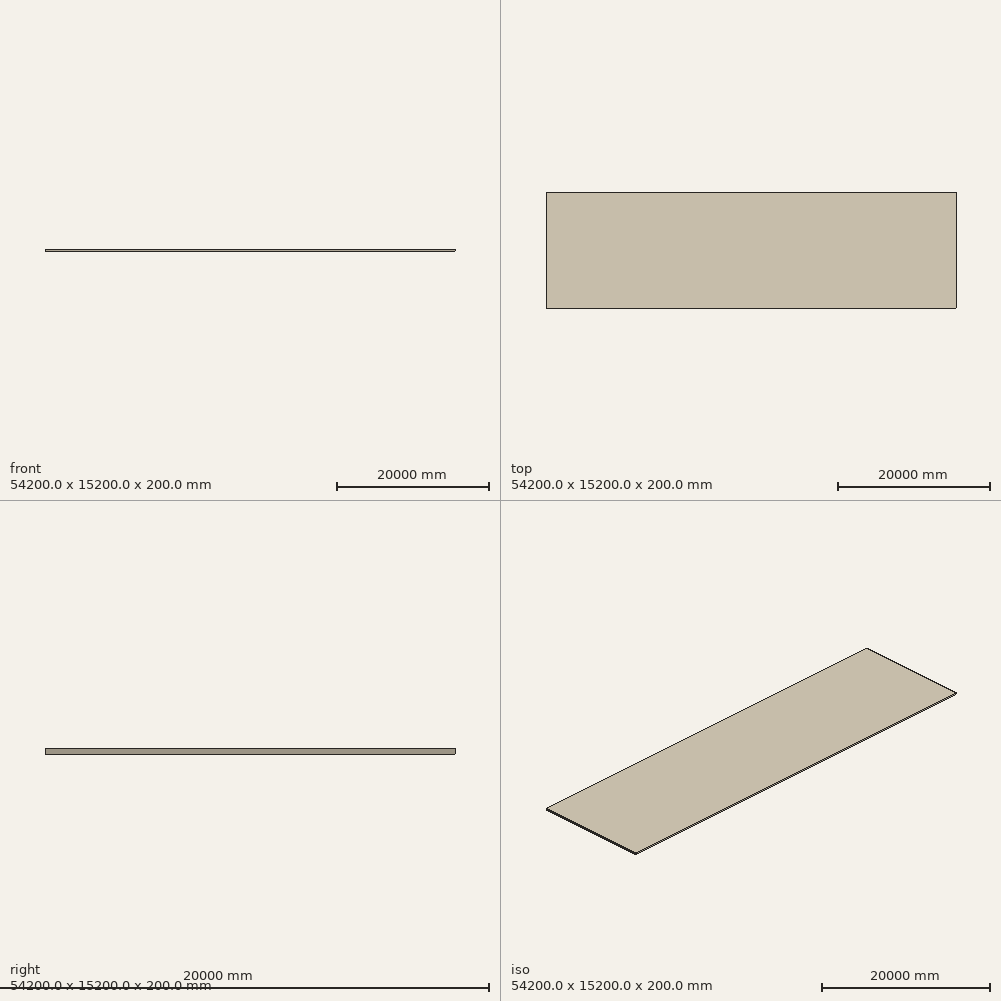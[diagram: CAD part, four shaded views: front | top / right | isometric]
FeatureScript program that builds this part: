
annotation { "Feature Type Name" : "Feature", "Feature Type Description" : "" }
export const myFeature = defineFeature(function(context is Context, id is Id, definition is map)
    precondition{}
    {
        {
            var Q0;
            Q0=qCreatedBy(makeId("Top.planeOp"),FACE);
            var sketch = newSketch(context, id + "F0", { "sketchPlane" : qUnion([Q0])});
            skLineSegment(sketch, "E0.bottom", {"start": v(0, 0) * mm, "end": v(54200, 0) * mm});
            skLineSegment(sketch, "E0.top", {"start": v(0, 15200) * mm, "end": v(54200, 15200) * mm});
            skLineSegment(sketch, "E0.left", {"start": v(0, 0) * mm, "end": v(0, 15200) * mm});
            skLineSegment(sketch, "E0.right", {"start": v(54200, 0) * mm, "end": v(54200, 15200) * mm});
            skSolve(sketch);
        }
        {
            var Q0;
            Q0 = qSketchRegion(id + "F0", true);
            extrude(context, id + "F1", {"entities" : qUnion([Q0]), "oppositeDirection" : true, "depth" : 200 * mm});
        }
    });
